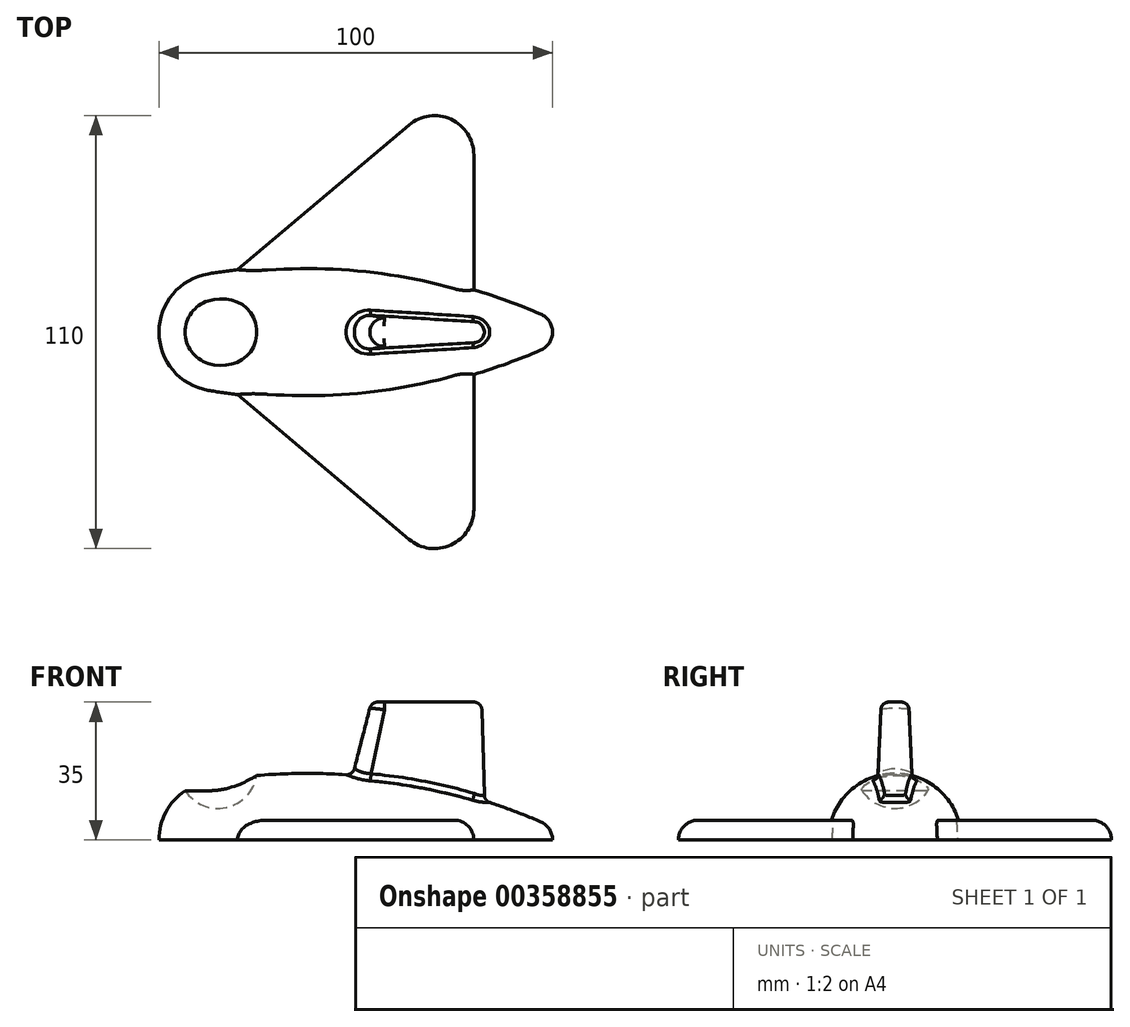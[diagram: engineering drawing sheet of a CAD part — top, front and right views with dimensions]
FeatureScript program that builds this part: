
annotation { "Feature Type Name" : "Feature", "Feature Type Description" : "" }
export const myFeature = defineFeature(function(context is Context, id is Id, definition is map)
    precondition{}
    {
        {
            var Q0;
            Q0=qCreatedBy(makeId("Front.planeOp"),FACE);
            var sketch = newSketch(context, id + "F0", { "sketchPlane" : qUnion([Q0])});
            skArc(sketch, "E0", {"start": v(-2.5, 14.8) * mm, "mid": v(-11.46, 9.68) * mm, "end": v(-15, 0) * mm});
            skArc(sketch, "E1", {"start": v(85, 0) * mm, "mid": v(84.18, 2.75) * mm, "end": v(81.98, 4.6) * mm});
            skArc(sketch, "E2", {"start": v(81.98, 4.6) * mm, "mid": v(40.48, 15.8) * mm, "end": v(-2.5, 14.8) * mm});
            skLineSegment(sketch, "E3", {"start": v(-15, 0) * mm, "end": v(85, 0) * mm});
            skSolve(sketch);
        }
        {
            var Q0;
            Q0=makeQuery(id+"F0.imprint","IMPRINT",FACE,{"disambiguationData":[TD([[makeQuery(id+"F0.imprint","IMPRINT",EDGE,{"derivedFrom":sQuery(id+"F0.wireOp",EDGE,"E0")}),1.0]])]});
            var Q1;
            Q1=sQuery(id+"F0.wireOp",EDGE,"E3");
            revolve(context, id + "F1", {"entities" : qUnion([Q0]), "axis" : qUnion([Q1]), "revolveType" : RevolveType.SYMMETRIC, "angle" : 180 * degree});
        }
        {
            var Q0;
            Q0=qCreatedBy(makeId("Front.planeOp"),FACE);
            var sketch = newSketch(context, id + "F2", { "sketchPlane" : qUnion([Q0])});
            skArc(sketch, "E4", {"start": v(-10, 18) * mm, "mid": v(0, 8) * mm, "end": v(10, 18) * mm});
            skLineSegment(sketch, "E5", {"start": v(-10, 18) * mm, "end": v(10, 18) * mm});
            skSolve(sketch);
        }
        {
            var Q0;
            Q0=makeQuery(id+"F2.imprint","IMPRINT",FACE,{"disambiguationData":[TD([[makeQuery(id+"F2.imprint","IMPRINT",EDGE,{"derivedFrom":sQuery(id+"F2.wireOp",EDGE,"E4")}),1.0]])]});
            var Q1;
            Q1=sQuery(id+"F2.wireOp",EDGE,"E5");
            revolve(context, id + "F3", {"operationType" : NewBodyOperationType.REMOVE, "entities" : qUnion([Q0]), "axis" : qUnion([Q1]), "revolveType" : RevolveType.FULL, "oppositeDirection" : true});
        }
        {
            var Q0;
            Q0=qCreatedBy(makeId("Top.planeOp"),FACE);
            var sketch = newSketch(context, id + "F4", { "sketchPlane" : qUnion([Q0])});
            skArc(sketch, "E6", {"start": v(35.33, 4.99) * mm, "mid": v(30, 0) * mm, "end": v(35.33, -4.99) * mm});
            skArc(sketch, "E7", {"start": v(65.2, -3) * mm, "mid": v(68, 0) * mm, "end": v(65.2, 3) * mm});
            skLineSegment(sketch, "E8", {"start": v(35.33, -4.99) * mm, "end": v(65.2, -3) * mm});
            skLineSegment(sketch, "E9.MirrorCS", {"start": v(35.33, 4.99) * mm, "end": v(65.2, 3) * mm});
            skSolve(sketch);
        }
        {
            var Q0;
            Q0=qCreatedBy(makeId("Top.planeOp"),FACE);
            cPlane(context, id + "F5", {"entities" : qUnion([Q0]), "cplaneType" : CPlaneType.OFFSET, "offset" : 35 * mm, "width" : 150 * mm, "height" : 150 * mm});
        }
        {
            var Q0;
            Q0=qCreatedBy(id+"F5.planeOp",FACE);
            var sketch = newSketch(context, id + "F6", { "sketchPlane" : qUnion([Q0])});
            skArc(sketch, "E10", {"start": v(65.13, -2) * mm, "mid": v(67, 0) * mm, "end": v(65.13, 2) * mm});
            skArc(sketch, "E11", {"start": v(42.73, 3.5) * mm, "mid": v(39, 0) * mm, "end": v(42.73, -3.5) * mm});
            skLineSegment(sketch, "E12", {"start": v(42.73, -3.5) * mm, "end": v(65.13, -2) * mm});
            skLineSegment(sketch, "E13.MirrorCS", {"start": v(42.73, 3.5) * mm, "end": v(65.13, 2) * mm});
            skSolve(sketch);
        }
        {
            var Q1;
            Q1=makeQuery(id+"F4.imprint","IMPRINT",FACE,{"disambiguationData":[TD([[makeQuery(id+"F4.imprint","IMPRINT",EDGE,{"derivedFrom":sQuery(id+"F4.wireOp",EDGE,"E6")}),1.0]])]});
            var Q2;
            Q2=makeQuery(id+"F6.imprint","IMPRINT",FACE,{"disambiguationData":[TD([[makeQuery(id+"F6.imprint","IMPRINT",EDGE,{"derivedFrom":sQuery(id+"F6.wireOp",EDGE,"E10")}),1.0]])]});
            loft(context, id + "F7", {"operationType" : NewBodyOperationType.ADD, "sheetProfilesArray" : [{ "sheetProfileEntities" : qUnion([Q1]) }, { "sheetProfileEntities" : qUnion([Q2]) }]});
        }
        {
            var Q0;
            Q0=makeQuery(id+"F7.boolean.opBoolean","INTERSECT",EDGE,{"derivedFrom":[makeQuery(id+"F1.opRevolve","SWEPT_FACE",FACE,{"disambiguationData":[OSD([sQuery(id+"F0.wireOp",EDGE,"E2")])]}),makeQuery(id+"F7.opLoft","SWEPT_FACE",FACE,{"disambiguationData":[OSD([sQuery(id+"F4.wireOp",EDGE,"E6"),sQuery(id+"F4.wireOp",EDGE,"E7"),sQuery(id+"F4.wireOp",EDGE,"E8"),sQuery(id+"F6.wireOp",EDGE,"E10"),sQuery(id+"F6.wireOp",EDGE,"E11"),sQuery(id+"F6.wireOp",EDGE,"E12")])]})]});
            var Q1;
            Q1=makeQuery(id+"F7.opLoft","MID_CAP_EDGE",EDGE,{"disambiguationData":[OSD([sQuery(id+"F6.wireOp",EDGE,"E10"),sQuery(id+"F6.wireOp",EDGE,"E11"),sQuery(id+"F6.wireOp",EDGE,"E12")])],"capPos":1.0});
            fillet(context, id + "F8", {"entities" : qUnion([Q0, Q1]), "radius" : 2 * mm, "tangentPropagation" : true, "allowEdgeOverflow" : false});
        }
        {
            var Q0;
            Q0=qCreatedBy(makeId("Top.planeOp"),FACE);
            var sketch = newSketch(context, id + "F9", { "sketchPlane" : qUnion([Q0])});
            skLineSegment(sketch, "E14", {"start": v(0, 11.64) * mm, "end": v(48.55, 52.64) * mm});
            skLineSegment(sketch, "E15", {"start": v(65, 45) * mm, "end": v(65, 3.92) * mm});
            skLineSegment(sketch, "E16", {"start": v(65, 3.92) * mm, "end": v(0, 11.64) * mm});
            skArc(sketch, "E17.0", {"start": v(81.98, 4.6) * mm, "mid": v(40.48, 15.8) * mm, "end": v(-2.5, 14.8) * mm});
            skPoint(sketch, "E18", {"position": v(5, 15.86) * mm});
            skPoint(sketch, "E19.visualSharp", {"position": v(65, 66.53) * mm});
            skArc(sketch, "E19.filletArc", {"start": v(65, 45) * mm, "mid": v(59.21, 54.07) * mm, "end": v(48.55, 52.64) * mm});
            skSolve(sketch);
        }
        {
            var Q0;
            {var subQ0=sQuery(id+"F9.wireOp",EDGE,"E19.filletArc");Q0=makeQuery(id+"F9.imprint","IMPRINT",FACE,{"disambiguationData":[TD([[makeQuery(id+"F9.imprint","IMPRINT",EDGE,{"derivedFrom":subQ0}),1.0]])]});}
            var Q1;
            {var subQ0=sQuery(id+"F9.wireOp",EDGE,"E16");Q1=makeQuery(id+"F9.imprint","IMPRINT",FACE,{"disambiguationData":[TD([[makeQuery(id+"F9.imprint","IMPRINT",EDGE,{"derivedFrom":subQ0}),-1.0]])]});}
            extrude(context, id + "F10", {"entities" : qUnion([Q0, Q1]), "operationType" : NewBodyOperationType.ADD, "depth" : 5 * mm});
        }
        {
            var Q0;
            Q0=makeQuery(id+"F1.opRevolve","SWEPT_BODY",BODY,{"disambiguationData":[OSD([sQuery(id+"F0.wireOp",EDGE,"E0"),sQuery(id+"F0.wireOp",EDGE,"E1"),sQuery(id+"F0.wireOp",EDGE,"E2"),sQuery(id+"F0.wireOp",EDGE,"E3")])]});
            var Q1;
            Q1=qCreatedBy(makeId("Front.planeOp"),FACE);
            mirror(context, id + "F11", {"operationType" : NewBodyOperationType.ADD, "entities" : qUnion([Q0]), "mirrorPlane" : qUnion([Q1])});
        }
        {
            var Q0;
            Q0=makeQuery(id+"F10.opExtrude","CAP_EDGE",EDGE,{"disambiguationData":[OSD([sQuery(id+"F9.wireOp",EDGE,"E15")])],"isStart":false});
            var Q1;
            Q1=makeQuery(id+"F11.opPattern","COPY",EDGE,{"derivedFrom":makeQuery(id+"F10.opExtrude","CAP_EDGE",EDGE,{"disambiguationData":[OSD([sQuery(id+"F9.wireOp",EDGE,"E15")])],"isStart":false}),"instanceName":"1"});
            fillet(context, id + "F12", {"entities" : qUnion([Q0, Q1]), "radius" : 5 * mm, "tangentPropagation" : true, "allowEdgeOverflow" : false});
        }
    });
